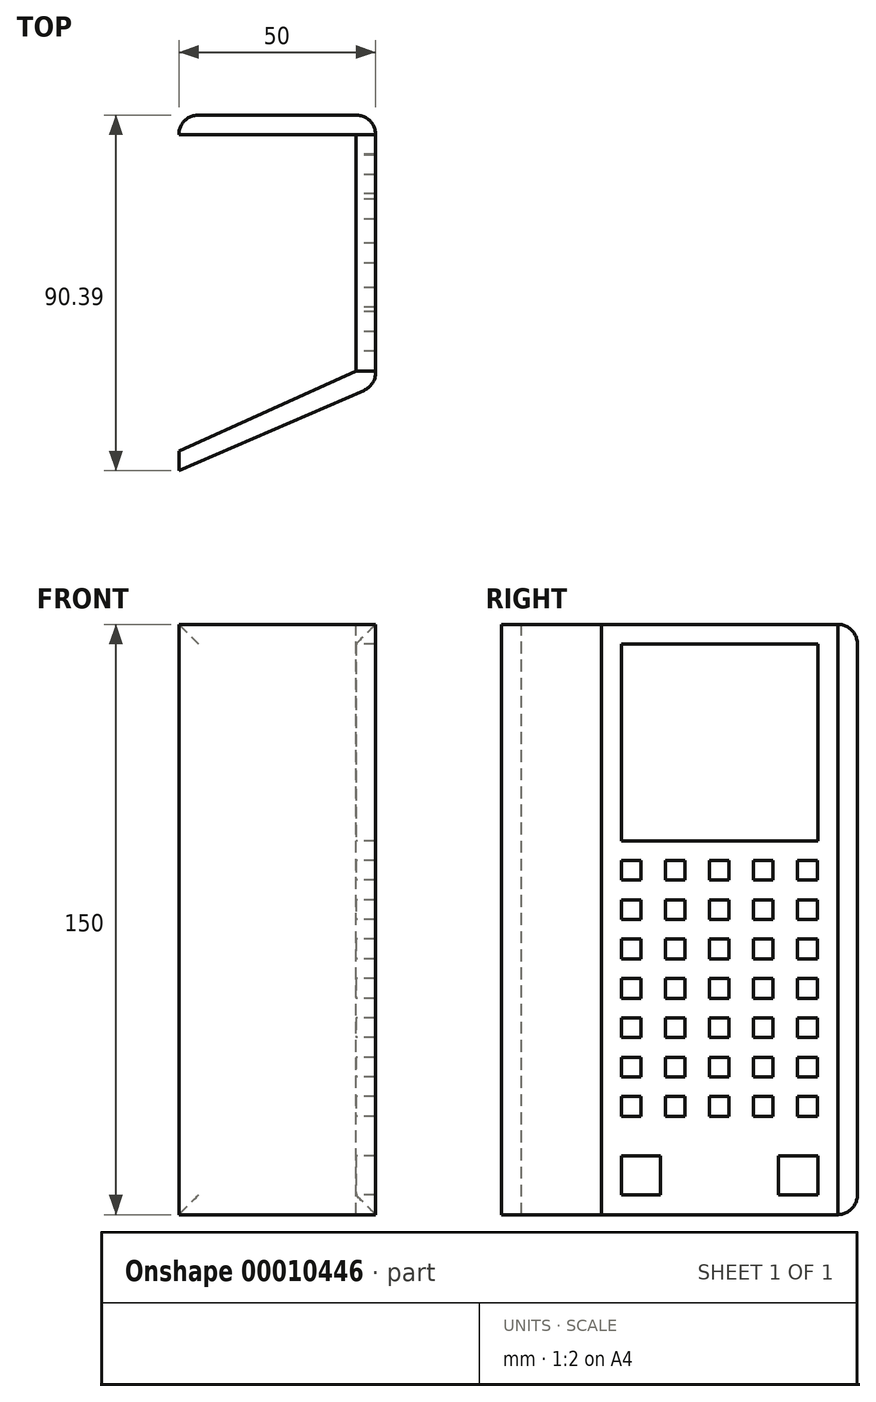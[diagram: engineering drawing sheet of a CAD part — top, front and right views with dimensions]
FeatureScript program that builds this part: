
annotation { "Feature Type Name" : "Feature", "Feature Type Description" : "" }
export const myFeature = defineFeature(function(context is Context, id is Id, definition is map)
    precondition{}
    {
        {
            var Q0;
            Q0=qCreatedBy(makeId("Right.planeOp"),FACE);
            var sketch = newSketch(context, id + "F0", { "sketchPlane" : qUnion([Q0])});
            skLineSegment(sketch, "E0.bottom", {"start": v(-27.28, 39.27) * mm, "end": v(32.72, 39.27) * mm});
            skLineSegment(sketch, "E0.top", {"start": v(-27.28, -110.73) * mm, "end": v(32.72, -110.73) * mm});
            skLineSegment(sketch, "E0.left", {"start": v(-27.28, 39.27) * mm, "end": v(-27.28, -110.73) * mm});
            skLineSegment(sketch, "E0.right", {"start": v(32.72, 39.27) * mm, "end": v(32.72, -110.73) * mm});
            skLineSegment(sketch, "E1.bottom", {"start": v(-22.28, 34.27) * mm, "end": v(27.72, 34.27) * mm});
            skLineSegment(sketch, "E1.top", {"start": v(-22.28, -15.73) * mm, "end": v(27.72, -15.73) * mm});
            skLineSegment(sketch, "E1.left", {"start": v(-22.28, 34.27) * mm, "end": v(-22.28, -15.73) * mm});
            skLineSegment(sketch, "E1.right", {"start": v(27.72, 34.27) * mm, "end": v(27.72, -15.73) * mm});
            skLineSegment(sketch, "E2.bottom", {"start": v(-22.28, -105.73) * mm, "end": v(-12.28, -105.73) * mm});
            skLineSegment(sketch, "E2.top", {"start": v(-22.28, -95.73) * mm, "end": v(-12.28, -95.73) * mm});
            skLineSegment(sketch, "E2.left", {"start": v(-22.28, -105.73) * mm, "end": v(-22.28, -95.73) * mm});
            skLineSegment(sketch, "E2.right", {"start": v(-12.28, -105.73) * mm, "end": v(-12.28, -95.73) * mm});
            skLineSegment(sketch, "E3.bottom", {"start": v(17.72, -95.73) * mm, "end": v(27.72, -95.73) * mm});
            skLineSegment(sketch, "E3.top", {"start": v(17.72, -105.73) * mm, "end": v(27.72, -105.73) * mm});
            skLineSegment(sketch, "E3.left", {"start": v(17.72, -95.73) * mm, "end": v(17.72, -105.73) * mm});
            skLineSegment(sketch, "E3.right", {"start": v(27.72, -95.73) * mm, "end": v(27.72, -105.73) * mm});
            skLineSegment(sketch, "E4.bottom", {"start": v(-22.28, -20.73) * mm, "end": v(-17.28, -20.73) * mm});
            skLineSegment(sketch, "E4.top", {"start": v(-22.28, -25.73) * mm, "end": v(-17.28, -25.73) * mm});
            skLineSegment(sketch, "E4.left", {"start": v(-22.28, -20.73) * mm, "end": v(-22.28, -25.73) * mm});
            skLineSegment(sketch, "E4.right", {"start": v(-17.28, -20.73) * mm, "end": v(-17.28, -25.73) * mm});
            skLineSegment(sketch, "E5.0.1.0", {"start": v(-22.28, -30.73) * mm, "end": v(-22.28, -35.73) * mm});
            skLineSegment(sketch, "E5.0.1.1", {"start": v(-22.28, -30.73) * mm, "end": v(-17.28, -30.73) * mm});
            skLineSegment(sketch, "E5.0.1.2", {"start": v(-17.28, -30.73) * mm, "end": v(-17.28, -35.73) * mm});
            skLineSegment(sketch, "E5.0.1.3", {"start": v(-22.28, -35.73) * mm, "end": v(-17.28, -35.73) * mm});
            skLineSegment(sketch, "E5.0.2.0", {"start": v(-22.28, -40.73) * mm, "end": v(-22.28, -45.73) * mm});
            skLineSegment(sketch, "E5.0.2.1", {"start": v(-22.28, -40.73) * mm, "end": v(-17.28, -40.73) * mm});
            skLineSegment(sketch, "E5.0.2.2", {"start": v(-17.28, -40.73) * mm, "end": v(-17.28, -45.73) * mm});
            skLineSegment(sketch, "E5.0.2.3", {"start": v(-22.28, -45.73) * mm, "end": v(-17.28, -45.73) * mm});
            skLineSegment(sketch, "E5.0.3.0", {"start": v(-22.28, -50.73) * mm, "end": v(-22.28, -55.73) * mm});
            skLineSegment(sketch, "E5.0.3.1", {"start": v(-22.28, -50.73) * mm, "end": v(-17.28, -50.73) * mm});
            skLineSegment(sketch, "E5.0.3.2", {"start": v(-17.28, -50.73) * mm, "end": v(-17.28, -55.73) * mm});
            skLineSegment(sketch, "E5.0.3.3", {"start": v(-22.28, -55.73) * mm, "end": v(-17.28, -55.73) * mm});
            skLineSegment(sketch, "E5.0.4.0", {"start": v(-22.28, -60.73) * mm, "end": v(-22.28, -65.73) * mm});
            skLineSegment(sketch, "E5.0.4.1", {"start": v(-22.28, -60.73) * mm, "end": v(-17.28, -60.73) * mm});
            skLineSegment(sketch, "E5.0.4.2", {"start": v(-17.28, -60.73) * mm, "end": v(-17.28, -65.73) * mm});
            skLineSegment(sketch, "E5.0.4.3", {"start": v(-22.28, -65.73) * mm, "end": v(-17.28, -65.73) * mm});
            skLineSegment(sketch, "E5.0.5.0", {"start": v(-22.28, -70.73) * mm, "end": v(-22.28, -75.73) * mm});
            skLineSegment(sketch, "E5.0.5.1", {"start": v(-22.28, -70.73) * mm, "end": v(-17.28, -70.73) * mm});
            skLineSegment(sketch, "E5.0.5.2", {"start": v(-17.28, -70.73) * mm, "end": v(-17.28, -75.73) * mm});
            skLineSegment(sketch, "E5.0.5.3", {"start": v(-22.28, -75.73) * mm, "end": v(-17.28, -75.73) * mm});
            skLineSegment(sketch, "E5.0.6.0", {"start": v(-22.28, -80.73) * mm, "end": v(-22.28, -85.73) * mm});
            skLineSegment(sketch, "E5.0.6.1", {"start": v(-22.28, -80.73) * mm, "end": v(-17.28, -80.73) * mm});
            skLineSegment(sketch, "E5.0.6.2", {"start": v(-17.28, -80.73) * mm, "end": v(-17.28, -85.73) * mm});
            skLineSegment(sketch, "E5.0.6.3", {"start": v(-22.28, -85.73) * mm, "end": v(-17.28, -85.73) * mm});
            skLineSegment(sketch, "E5.1.0.0", {"start": v(-11.08, -20.73) * mm, "end": v(-11.08, -25.73) * mm});
            skLineSegment(sketch, "E5.1.0.1", {"start": v(-11.08, -20.73) * mm, "end": v(-6.08, -20.73) * mm});
            skLineSegment(sketch, "E5.1.0.2", {"start": v(-6.08, -20.73) * mm, "end": v(-6.08, -25.73) * mm});
            skLineSegment(sketch, "E5.1.0.3", {"start": v(-11.08, -25.73) * mm, "end": v(-6.08, -25.73) * mm});
            skLineSegment(sketch, "E5.1.1.0", {"start": v(-11.08, -30.73) * mm, "end": v(-11.08, -35.73) * mm});
            skLineSegment(sketch, "E5.1.1.1", {"start": v(-11.08, -30.73) * mm, "end": v(-6.08, -30.73) * mm});
            skLineSegment(sketch, "E5.1.1.2", {"start": v(-6.08, -30.73) * mm, "end": v(-6.08, -35.73) * mm});
            skLineSegment(sketch, "E5.1.1.3", {"start": v(-11.08, -35.73) * mm, "end": v(-6.08, -35.73) * mm});
            skLineSegment(sketch, "E5.1.2.0", {"start": v(-11.08, -40.73) * mm, "end": v(-11.08, -45.73) * mm});
            skLineSegment(sketch, "E5.1.2.1", {"start": v(-11.08, -40.73) * mm, "end": v(-6.08, -40.73) * mm});
            skLineSegment(sketch, "E5.1.2.2", {"start": v(-6.08, -40.73) * mm, "end": v(-6.08, -45.73) * mm});
            skLineSegment(sketch, "E5.1.2.3", {"start": v(-11.08, -45.73) * mm, "end": v(-6.08, -45.73) * mm});
            skLineSegment(sketch, "E5.1.3.0", {"start": v(-11.08, -50.73) * mm, "end": v(-11.08, -55.73) * mm});
            skLineSegment(sketch, "E5.1.3.1", {"start": v(-11.08, -50.73) * mm, "end": v(-6.08, -50.73) * mm});
            skLineSegment(sketch, "E5.1.3.2", {"start": v(-6.08, -50.73) * mm, "end": v(-6.08, -55.73) * mm});
            skLineSegment(sketch, "E5.1.3.3", {"start": v(-11.08, -55.73) * mm, "end": v(-6.08, -55.73) * mm});
            skLineSegment(sketch, "E5.1.4.0", {"start": v(-11.08, -60.73) * mm, "end": v(-11.08, -65.73) * mm});
            skLineSegment(sketch, "E5.1.4.1", {"start": v(-11.08, -60.73) * mm, "end": v(-6.08, -60.73) * mm});
            skLineSegment(sketch, "E5.1.4.2", {"start": v(-6.08, -60.73) * mm, "end": v(-6.08, -65.73) * mm});
            skLineSegment(sketch, "E5.1.4.3", {"start": v(-11.08, -65.73) * mm, "end": v(-6.08, -65.73) * mm});
            skLineSegment(sketch, "E5.1.5.0", {"start": v(-11.08, -70.73) * mm, "end": v(-11.08, -75.73) * mm});
            skLineSegment(sketch, "E5.1.5.1", {"start": v(-11.08, -70.73) * mm, "end": v(-6.08, -70.73) * mm});
            skLineSegment(sketch, "E5.1.5.2", {"start": v(-6.08, -70.73) * mm, "end": v(-6.08, -75.73) * mm});
            skLineSegment(sketch, "E5.1.5.3", {"start": v(-11.08, -75.73) * mm, "end": v(-6.08, -75.73) * mm});
            skLineSegment(sketch, "E5.1.6.0", {"start": v(-11.08, -80.73) * mm, "end": v(-11.08, -85.73) * mm});
            skLineSegment(sketch, "E5.1.6.1", {"start": v(-11.08, -80.73) * mm, "end": v(-6.08, -80.73) * mm});
            skLineSegment(sketch, "E5.1.6.2", {"start": v(-6.08, -80.73) * mm, "end": v(-6.08, -85.73) * mm});
            skLineSegment(sketch, "E5.1.6.3", {"start": v(-11.08, -85.73) * mm, "end": v(-6.08, -85.73) * mm});
            skLineSegment(sketch, "E5.2.0.0", {"start": v(0.12, -20.73) * mm, "end": v(0.12, -25.73) * mm});
            skLineSegment(sketch, "E5.2.0.1", {"start": v(0.12, -20.73) * mm, "end": v(5.12, -20.73) * mm});
            skLineSegment(sketch, "E5.2.0.2", {"start": v(5.12, -20.73) * mm, "end": v(5.12, -25.73) * mm});
            skLineSegment(sketch, "E5.2.0.3", {"start": v(0.12, -25.73) * mm, "end": v(5.12, -25.73) * mm});
            skLineSegment(sketch, "E5.2.1.0", {"start": v(0.12, -30.73) * mm, "end": v(0.12, -35.73) * mm});
            skLineSegment(sketch, "E5.2.1.1", {"start": v(0.12, -30.73) * mm, "end": v(5.12, -30.73) * mm});
            skLineSegment(sketch, "E5.2.1.2", {"start": v(5.12, -30.73) * mm, "end": v(5.12, -35.73) * mm});
            skLineSegment(sketch, "E5.2.1.3", {"start": v(0.12, -35.73) * mm, "end": v(5.12, -35.73) * mm});
            skLineSegment(sketch, "E5.2.2.0", {"start": v(0.12, -40.73) * mm, "end": v(0.12, -45.73) * mm});
            skLineSegment(sketch, "E5.2.2.1", {"start": v(0.12, -40.73) * mm, "end": v(5.12, -40.73) * mm});
            skLineSegment(sketch, "E5.2.2.2", {"start": v(5.12, -40.73) * mm, "end": v(5.12, -45.73) * mm});
            skLineSegment(sketch, "E5.2.2.3", {"start": v(0.12, -45.73) * mm, "end": v(5.12, -45.73) * mm});
            skLineSegment(sketch, "E5.2.3.0", {"start": v(0.12, -50.73) * mm, "end": v(0.12, -55.73) * mm});
            skLineSegment(sketch, "E5.2.3.1", {"start": v(0.12, -50.73) * mm, "end": v(5.12, -50.73) * mm});
            skLineSegment(sketch, "E5.2.3.2", {"start": v(5.12, -50.73) * mm, "end": v(5.12, -55.73) * mm});
            skLineSegment(sketch, "E5.2.3.3", {"start": v(0.12, -55.73) * mm, "end": v(5.12, -55.73) * mm});
            skLineSegment(sketch, "E5.2.4.0", {"start": v(0.12, -60.73) * mm, "end": v(0.12, -65.73) * mm});
            skLineSegment(sketch, "E5.2.4.1", {"start": v(0.12, -60.73) * mm, "end": v(5.12, -60.73) * mm});
            skLineSegment(sketch, "E5.2.4.2", {"start": v(5.12, -60.73) * mm, "end": v(5.12, -65.73) * mm});
            skLineSegment(sketch, "E5.2.4.3", {"start": v(0.12, -65.73) * mm, "end": v(5.12, -65.73) * mm});
            skLineSegment(sketch, "E5.2.5.0", {"start": v(0.12, -70.73) * mm, "end": v(0.12, -75.73) * mm});
            skLineSegment(sketch, "E5.2.5.1", {"start": v(0.12, -70.73) * mm, "end": v(5.12, -70.73) * mm});
            skLineSegment(sketch, "E5.2.5.2", {"start": v(5.12, -70.73) * mm, "end": v(5.12, -75.73) * mm});
            skLineSegment(sketch, "E5.2.5.3", {"start": v(0.12, -75.73) * mm, "end": v(5.12, -75.73) * mm});
            skLineSegment(sketch, "E5.2.6.0", {"start": v(0.12, -80.73) * mm, "end": v(0.12, -85.73) * mm});
            skLineSegment(sketch, "E5.2.6.1", {"start": v(0.12, -80.73) * mm, "end": v(5.12, -80.73) * mm});
            skLineSegment(sketch, "E5.2.6.2", {"start": v(5.12, -80.73) * mm, "end": v(5.12, -85.73) * mm});
            skLineSegment(sketch, "E5.2.6.3", {"start": v(0.12, -85.73) * mm, "end": v(5.12, -85.73) * mm});
            skLineSegment(sketch, "E5.3.0.0", {"start": v(11.32, -20.73) * mm, "end": v(11.32, -25.73) * mm});
            skLineSegment(sketch, "E5.3.0.1", {"start": v(11.32, -20.73) * mm, "end": v(16.32, -20.73) * mm});
            skLineSegment(sketch, "E5.3.0.2", {"start": v(16.32, -20.73) * mm, "end": v(16.32, -25.73) * mm});
            skLineSegment(sketch, "E5.3.0.3", {"start": v(11.32, -25.73) * mm, "end": v(16.32, -25.73) * mm});
            skLineSegment(sketch, "E5.3.1.0", {"start": v(11.32, -30.73) * mm, "end": v(11.32, -35.73) * mm});
            skLineSegment(sketch, "E5.3.1.1", {"start": v(11.32, -30.73) * mm, "end": v(16.32, -30.73) * mm});
            skLineSegment(sketch, "E5.3.1.2", {"start": v(16.32, -30.73) * mm, "end": v(16.32, -35.73) * mm});
            skLineSegment(sketch, "E5.3.1.3", {"start": v(11.32, -35.73) * mm, "end": v(16.32, -35.73) * mm});
            skLineSegment(sketch, "E5.3.2.0", {"start": v(11.32, -40.73) * mm, "end": v(11.32, -45.73) * mm});
            skLineSegment(sketch, "E5.3.2.1", {"start": v(11.32, -40.73) * mm, "end": v(16.32, -40.73) * mm});
            skLineSegment(sketch, "E5.3.2.2", {"start": v(16.32, -40.73) * mm, "end": v(16.32, -45.73) * mm});
            skLineSegment(sketch, "E5.3.2.3", {"start": v(11.32, -45.73) * mm, "end": v(16.32, -45.73) * mm});
            skLineSegment(sketch, "E5.3.3.0", {"start": v(11.32, -50.73) * mm, "end": v(11.32, -55.73) * mm});
            skLineSegment(sketch, "E5.3.3.1", {"start": v(11.32, -50.73) * mm, "end": v(16.32, -50.73) * mm});
            skLineSegment(sketch, "E5.3.3.2", {"start": v(16.32, -50.73) * mm, "end": v(16.32, -55.73) * mm});
            skLineSegment(sketch, "E5.3.3.3", {"start": v(11.32, -55.73) * mm, "end": v(16.32, -55.73) * mm});
            skLineSegment(sketch, "E5.3.4.0", {"start": v(11.32, -60.73) * mm, "end": v(11.32, -65.73) * mm});
            skLineSegment(sketch, "E5.3.4.1", {"start": v(11.32, -60.73) * mm, "end": v(16.32, -60.73) * mm});
            skLineSegment(sketch, "E5.3.4.2", {"start": v(16.32, -60.73) * mm, "end": v(16.32, -65.73) * mm});
            skLineSegment(sketch, "E5.3.4.3", {"start": v(11.32, -65.73) * mm, "end": v(16.32, -65.73) * mm});
            skLineSegment(sketch, "E5.3.5.0", {"start": v(11.32, -70.73) * mm, "end": v(11.32, -75.73) * mm});
            skLineSegment(sketch, "E5.3.5.1", {"start": v(11.32, -70.73) * mm, "end": v(16.32, -70.73) * mm});
            skLineSegment(sketch, "E5.3.5.2", {"start": v(16.32, -70.73) * mm, "end": v(16.32, -75.73) * mm});
            skLineSegment(sketch, "E5.3.5.3", {"start": v(11.32, -75.73) * mm, "end": v(16.32, -75.73) * mm});
            skLineSegment(sketch, "E5.3.6.0", {"start": v(11.32, -80.73) * mm, "end": v(11.32, -85.73) * mm});
            skLineSegment(sketch, "E5.3.6.1", {"start": v(11.32, -80.73) * mm, "end": v(16.32, -80.73) * mm});
            skLineSegment(sketch, "E5.3.6.2", {"start": v(16.32, -80.73) * mm, "end": v(16.32, -85.73) * mm});
            skLineSegment(sketch, "E5.3.6.3", {"start": v(11.32, -85.73) * mm, "end": v(16.32, -85.73) * mm});
            skLineSegment(sketch, "E5.4.0.0", {"start": v(22.52, -20.73) * mm, "end": v(22.52, -25.73) * mm});
            skLineSegment(sketch, "E5.4.0.1", {"start": v(22.52, -20.73) * mm, "end": v(27.52, -20.73) * mm});
            skLineSegment(sketch, "E5.4.0.2", {"start": v(27.52, -20.73) * mm, "end": v(27.52, -25.73) * mm});
            skLineSegment(sketch, "E5.4.0.3", {"start": v(22.52, -25.73) * mm, "end": v(27.52, -25.73) * mm});
            skLineSegment(sketch, "E5.4.1.0", {"start": v(22.52, -30.73) * mm, "end": v(22.52, -35.73) * mm});
            skLineSegment(sketch, "E5.4.1.1", {"start": v(22.52, -30.73) * mm, "end": v(27.52, -30.73) * mm});
            skLineSegment(sketch, "E5.4.1.2", {"start": v(27.52, -30.73) * mm, "end": v(27.52, -35.73) * mm});
            skLineSegment(sketch, "E5.4.1.3", {"start": v(22.52, -35.73) * mm, "end": v(27.52, -35.73) * mm});
            skLineSegment(sketch, "E5.4.2.0", {"start": v(22.52, -40.73) * mm, "end": v(22.52, -45.73) * mm});
            skLineSegment(sketch, "E5.4.2.1", {"start": v(22.52, -40.73) * mm, "end": v(27.52, -40.73) * mm});
            skLineSegment(sketch, "E5.4.2.2", {"start": v(27.52, -40.73) * mm, "end": v(27.52, -45.73) * mm});
            skLineSegment(sketch, "E5.4.2.3", {"start": v(22.52, -45.73) * mm, "end": v(27.52, -45.73) * mm});
            skLineSegment(sketch, "E5.4.3.0", {"start": v(22.52, -50.73) * mm, "end": v(22.52, -55.73) * mm});
            skLineSegment(sketch, "E5.4.3.1", {"start": v(22.52, -50.73) * mm, "end": v(27.52, -50.73) * mm});
            skLineSegment(sketch, "E5.4.3.2", {"start": v(27.52, -50.73) * mm, "end": v(27.52, -55.73) * mm});
            skLineSegment(sketch, "E5.4.3.3", {"start": v(22.52, -55.73) * mm, "end": v(27.52, -55.73) * mm});
            skLineSegment(sketch, "E5.4.4.0", {"start": v(22.52, -60.73) * mm, "end": v(22.52, -65.73) * mm});
            skLineSegment(sketch, "E5.4.4.1", {"start": v(22.52, -60.73) * mm, "end": v(27.52, -60.73) * mm});
            skLineSegment(sketch, "E5.4.4.2", {"start": v(27.52, -60.73) * mm, "end": v(27.52, -65.73) * mm});
            skLineSegment(sketch, "E5.4.4.3", {"start": v(22.52, -65.73) * mm, "end": v(27.52, -65.73) * mm});
            skLineSegment(sketch, "E5.4.5.0", {"start": v(22.52, -70.73) * mm, "end": v(22.52, -75.73) * mm});
            skLineSegment(sketch, "E5.4.5.1", {"start": v(22.52, -70.73) * mm, "end": v(27.52, -70.73) * mm});
            skLineSegment(sketch, "E5.4.5.2", {"start": v(27.52, -70.73) * mm, "end": v(27.52, -75.73) * mm});
            skLineSegment(sketch, "E5.4.5.3", {"start": v(22.52, -75.73) * mm, "end": v(27.52, -75.73) * mm});
            skLineSegment(sketch, "E5.4.6.0", {"start": v(22.52, -80.73) * mm, "end": v(22.52, -85.73) * mm});
            skLineSegment(sketch, "E5.4.6.1", {"start": v(22.52, -80.73) * mm, "end": v(27.52, -80.73) * mm});
            skLineSegment(sketch, "E5.4.6.2", {"start": v(27.52, -80.73) * mm, "end": v(27.52, -85.73) * mm});
            skLineSegment(sketch, "E5.4.6.3", {"start": v(22.52, -85.73) * mm, "end": v(27.52, -85.73) * mm});
            skLineSegment(sketch, "E5.direction1", {"start": v(-22.28, -25.73) * mm, "end": v(-11.08, -25.73) * mm, "construction": true});
            skLineSegment(sketch, "E5.direction2", {"start": v(-22.28, -25.73) * mm, "end": v(-22.28, -35.73) * mm, "construction": true});
            skSolve(sketch);
        }
        {
            var Q0;
            Q0=makeQuery(id+"F0.imprint","IMPRINT",FACE,{"disambiguationData":[TD([[makeQuery(id+"F0.imprint","IMPRINT",EDGE,{"derivedFrom":sQuery(id+"F0.wireOp",EDGE,"E0.bottom")}),-1.0]])]});
            extrude(context, id + "F1", {"entities" : qUnion([Q0]), "depth" : 5 * mm});
        }
        {
            var Q0;
            Q0=makeQuery(id+"F1.opExtrude","SWEPT_FACE",FACE,{"disambiguationData":[OSD([sQuery(id+"F0.wireOp",EDGE,"E0.right")])]});
            var sketch = newSketch(context, id + "F2", { "sketchPlane" : qUnion([Q0])});
            skLineSegment(sketch, "E6.bottom", {"start": v(-5, 39.27) * mm, "end": v(45, 39.27) * mm});
            skLineSegment(sketch, "E6.top", {"start": v(-5, -110.73) * mm, "end": v(45, -110.73) * mm});
            skLineSegment(sketch, "E6.left", {"start": v(-5, 39.27) * mm, "end": v(-5, -110.73) * mm});
            skLineSegment(sketch, "E6.right", {"start": v(45, 39.27) * mm, "end": v(45, -110.73) * mm});
            skSolve(sketch);
        }
        {
            var Q0;
            Q0 = qSketchRegion(id + "F2", true);
            extrude(context, id + "F3", {"entities" : qUnion([Q0]), "depth" : 5 * mm});
        }
        {
            var Q0;
            Q0=makeQuery(id+"F3.opExtrude","CAP_FACE",FACE,{"disambiguationData":[OSD([sQuery(id+"F2.wireOp",EDGE,"E6.bottom"),sQuery(id+"F2.wireOp",EDGE,"E6.top"),sQuery(id+"F2.wireOp",EDGE,"E6.left"),sQuery(id+"F2.wireOp",EDGE,"E6.right")])],"isStart":false});
            fillet(context, id + "F4", {"entities" : qUnion([Q0]), "radius" : 5 * mm, "tangentPropagation" : true, "allowEdgeOverflow" : false});
        }
        {
            var Q0;
            Q0=makeQuery(id+"F1.opExtrude","SWEPT_FACE",FACE,{"disambiguationData":[OSD([sQuery(id+"F0.wireOp",EDGE,"E0.bottom")])]});
            var sketch = newSketch(context, id + "F5", { "sketchPlane" : qUnion([Q0])});
            skLineSegment(sketch, "E7.0", {"start": v(5, 32.72) * mm, "end": v(-45, 32.72) * mm});
            skLineSegment(sketch, "E8.0", {"start": v(5, -27.28) * mm, "end": v(0, -27.28) * mm});
            skLineSegment(sketch, "E9", {"start": v(5, -27.28) * mm, "end": v(5, -27.67) * mm});
            skLineSegment(sketch, "E10", {"start": v(2, -32.26) * mm, "end": v(-45, -52.67) * mm});
            skLineSegment(sketch, "E11", {"start": v(0, -27.28) * mm, "end": v(-45, -47.67) * mm});
            skLineSegment(sketch, "E12", {"start": v(-45, -47.67) * mm, "end": v(-45, -52.67) * mm});
            skPoint(sketch, "E13.visualSharp", {"position": v(5, -30.95) * mm});
            skArc(sketch, "E13.filletArc", {"start": v(2, -32.26) * mm, "mid": v(4.18, -30.41) * mm, "end": v(5, -27.67) * mm});
            skSolve(sketch);
        }
        {
            var Q0;
            Q0=makeQuery(id+"F5.imprint","IMPRINT",FACE,{"disambiguationData":[TD([[makeQuery(id+"F5.imprint","IMPRINT",EDGE,{"derivedFrom":sQuery(id+"F5.wireOp",EDGE,"E8.0")}),1.0]])]});
            extrude(context, id + "F6", {"entities" : qUnion([Q0]), "oppositeDirection" : true, "depth" : 150 * mm});
        }
    });
